# Revit family: PRD_FrankeWS_ShwrFttngsPckg_F5SlidingAdhesiveFlange_ACBX9002
name_source: partatom
category: Specialty Equipment
revit_build: Autodesk Revit 2018 (Build: 20190510_1515(x64)
units: mm (PartAtom-declared; Revit-internal decimal feet)

## family parameters
Always vertical = No
Cut with Voids When Loaded = No
OmniClass Number = 23.45.05.14.99
OmniClass Title = Other Sanitary Washing Plumbing Fixtures
Part Type = Normal
Room Calculation Point = No
Round Connector Dimension = Use Diameter
Shared = No
Work Plane-Based = Yes

## types (1)
- ACBX9002
    AssetType = Fixed
    BIMObjectName = PRD_AR_ShowerFittingsPackage_F5SlidingAdhesiveFlange_ACBX9002
    BodyMaterial = <By Category>
    Category = Pr_40_20_87_75, Shower fittings package
    Color = red
    Default Elevation = 1219 mm
    Description = Sliding adhesive flange, continuously-adjustable, with form-closed, flexible, 70 mm wide sealing collar. Sealing collar made of water-tight, permanently-elastic, alkali-resistant, and crack-bridging thermoplastic elastomer with polypropylene fleece for connecting to compound seals in dry and wet construction.
    DurationUnit = year
    Features = sealing collar made of water-tight, permanently-elastic, alkali-resistant, and crack-bridging thermoplastic elastomer with polypropylene fleece
    GrossWeight = 0.35 kg
    IfcExportAs = IfcSanitaryTerminalType
    IfcExportType = USERDEFINED
    Manufacturer = KWC Group AG
    ManufacturerName = KWC Group AG
    ManufacturerURL = www.kwc.com
    Material = elastomer
    Model = ACBX9002
    ModelNumber = 2030041606
    ModelReference = ACBX9002
    NBSDescription = Shower fittings package
    NBSReference = 45-35-70/330
    Name = F5 Sliding adhesive flange ACBX9002
    NetWeight = 0.33 kg
    NominalDepth = 0 mm  [stored 0 ft]
    NominalHeight = 360 mm  [stored 1.1811 ft]
    NominalLength = 0 mm  [stored 0 ft]
    NominalWidth = 310 mm  [stored 1.01706 ft]
    ProductCode = 210.0636.676
    ProductInformation = https://pim.kwc.com
    Quantity = 1
    QuantityUom = Piece
    Status = New
    TopMaterial = PRD_AR_Elastomer_Red
    URL = www.kwc.com
    Uniclass2015Code = Pr_40_20_87_75
    Uniclass2015Title = Shower fittings package
    Uniclass2015Version = Products v1.23
    Version = 1
    WarrantyDurationUnit = year

note: [stored X ft] marks values corroborated as IEEE doubles in the binary element streams (Revit-internal decimal feet)

## geometry (parser evidence)
native form markers: Sweep x3
no freeform markers — native parametric forms only
